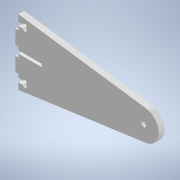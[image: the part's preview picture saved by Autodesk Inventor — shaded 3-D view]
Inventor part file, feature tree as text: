
AUTODESK INVENTOR PART (.ipt)
format: ipt  version: 2022 (Build 260153000, 153)  size: 164,864 bytes
history: native  units: mm
features: reference x8, other x5, extrude x3, sketch x3
ambient origin geometry x8: Origin, YZ Plane, XZ Plane, XY Plane, X Axis, Y Axis, Z Axis, Center Point
bodies: Solid1 (feature_tree)
feature tree (19):
  extrude  "Extrusion1"  Depth=150.0mm
  extrude  "Extrusion2"  Depth=136.046958mm
  extrude  "Extrusion3"  Depth=6.2mm TaperAngle=0.0deg
  sketch  "Sketch2"  dims[d0=5.0mm d1=150.0mm]
  reference  "Reference1"
  reference  "Reference2"
  reference  "Reference3"
  reference  "Reference4"
  reference  "Reference5"
  reference  "Reference6"
  reference  "Reference7"
  sketch  "Sketch4"  dims[d2=35.0mm d3=136.046958mm]
  sketch  "Sketch5"  dims[d4=32.066454mm d5=6.2mm d6=0.0mm d7=3.2mm d8=15.0mm d9=15.0mm d10=1.6mm d11=25.0mm d12=10.0mm d13=0.0mm d14=6.1mm d15=4.0mm d16=7.0mm d17=3.5mm d18=3.2mm d19=6.2mm d20=0.0mm]
  reference  "Reference8"
  other  "<userpath>\OneDrive\Escritorio\Mini_Proyecto_Diseno\Diseno_18012\Modelo_MPD\Carril.iam"
  other  "Carril.iam"
  other  "Eje_Carril:1"
  other  "Assembly_Final.iam"
  other  "Base_proyecto:1"
